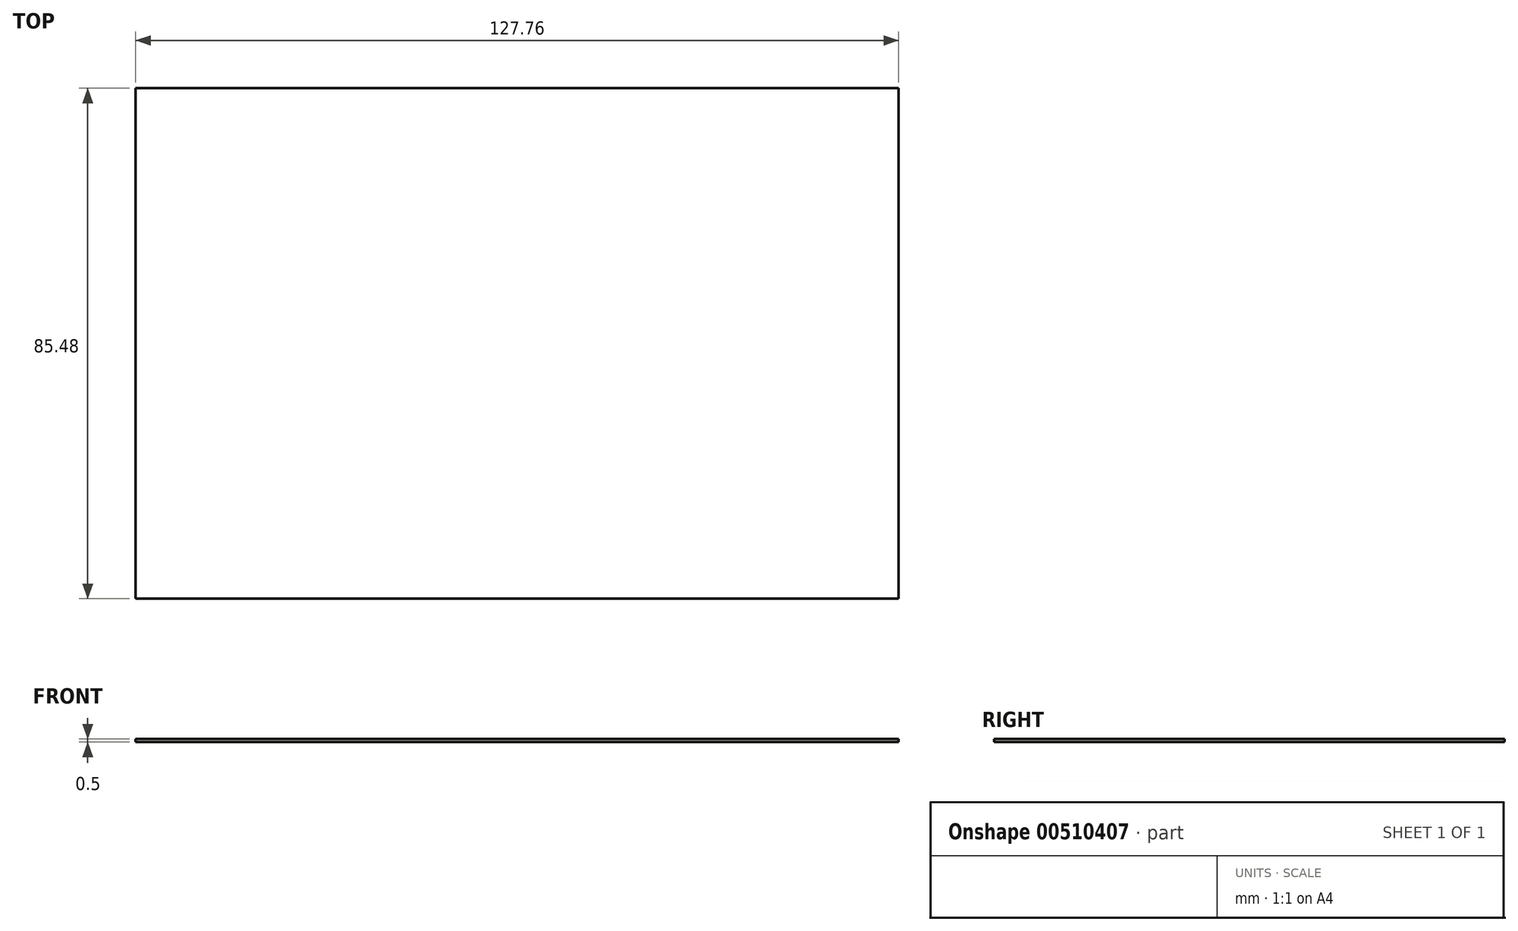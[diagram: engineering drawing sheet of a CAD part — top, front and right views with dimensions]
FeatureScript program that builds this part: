
annotation { "Feature Type Name" : "Feature", "Feature Type Description" : "" }
export const myFeature = defineFeature(function(context is Context, id is Id, definition is map)
    precondition{}
    {
        {
            var Q0;
            Q0=qCreatedBy(makeId("Top.planeOp"),FACE);
            var sketch = newSketch(context, id + "F0", { "sketchPlane" : qUnion([Q0])});
            skLineSegment(sketch, "E0.bottom", {"start": v(63.88, -42.74) * mm, "end": v(-63.88, -42.74) * mm});
            skLineSegment(sketch, "E0.top", {"start": v(63.88, 42.74) * mm, "end": v(-63.88, 42.74) * mm});
            skLineSegment(sketch, "E0.left", {"start": v(63.88, -42.74) * mm, "end": v(63.88, 42.74) * mm});
            skLineSegment(sketch, "E0.right", {"start": v(-63.88, -42.74) * mm, "end": v(-63.88, 42.74) * mm});
            skPoint(sketch, "E0.middle", {"position": v(0, 0) * mm});
            skSolve(sketch);
        }
        {
            var Q0;
            Q0=makeQuery(id+"F0.imprint","IMPRINT",FACE,{"disambiguationData":[TD([[makeQuery(id+"F0.imprint","IMPRINT",EDGE,{"derivedFrom":sQuery(id+"F0.wireOp",EDGE,"E0.bottom")}),-1.0]])]});
            extrude(context, id + "F1", {"entities" : qUnion([Q0]), "oppositeDirection" : true, "depth" : 0.5 * mm});
        }
    });
